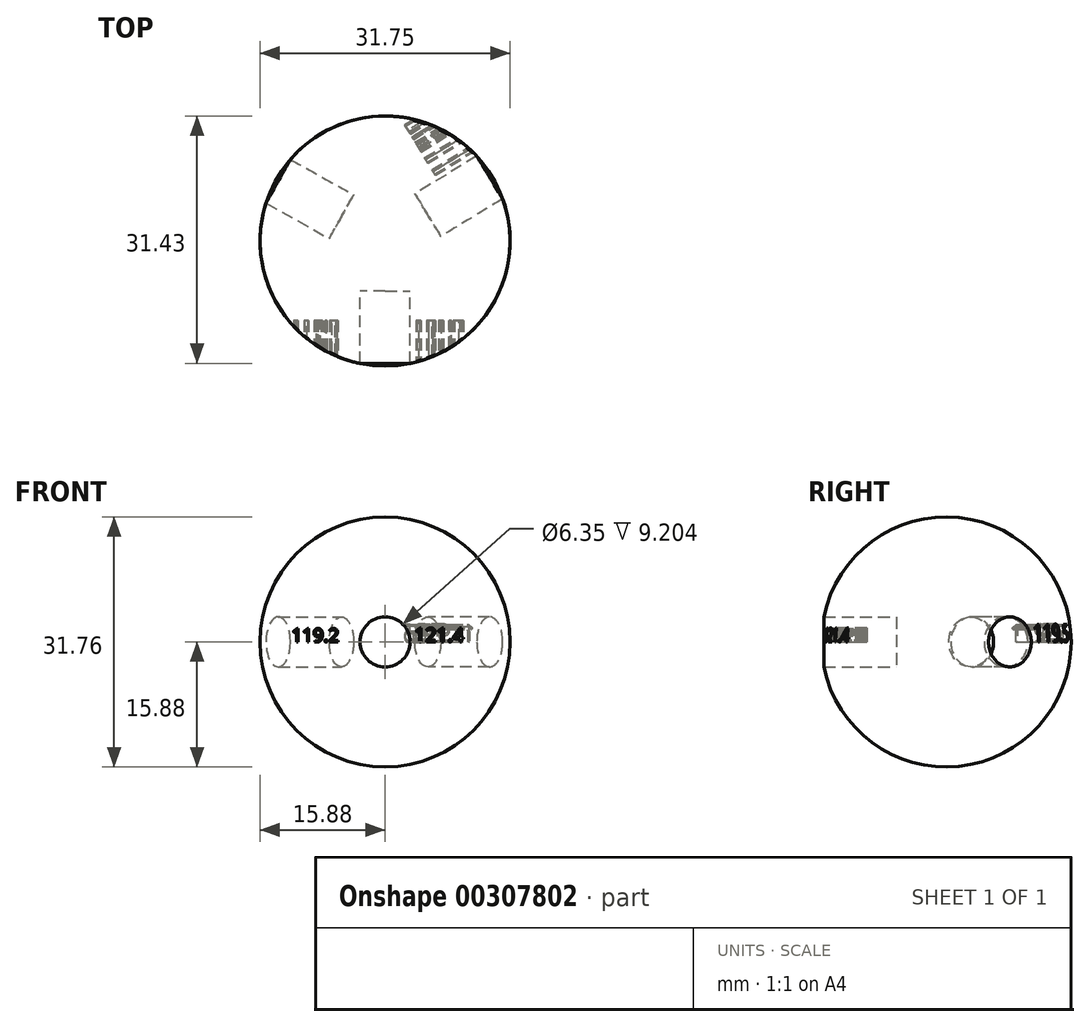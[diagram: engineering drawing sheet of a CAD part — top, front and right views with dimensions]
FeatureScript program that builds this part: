
annotation { "Feature Type Name" : "Feature", "Feature Type Description" : "" }
export const myFeature = defineFeature(function(context is Context, id is Id, definition is map)
    precondition{}
    {
        {
            var Q0;
            Q0=qCreatedBy(makeId("Top.planeOp"),FACE);
            var sketch = newSketch(context, id + "F0", { "sketchPlane" : qUnion([Q0])});
            skArc(sketch, "E0", {"start": v(0, 15.88) * mm, "mid": v(-15.88, 0) * mm, "end": v(0, -15.88) * mm});
            skLineSegment(sketch, "E1", {"start": v(0, 15.88) * mm, "end": v(0, -15.88) * mm});
            skSolve(sketch);
        }
        {
            var Q0;
            Q0=makeQuery(id+"F0.imprint","IMPRINT",FACE,{"disambiguationData":[TD([[makeQuery(id+"F0.imprint","IMPRINT",EDGE,{"derivedFrom":sQuery(id+"F0.wireOp",EDGE,"E0")}),1.0]])]});
            var Q1;
            Q1=sQuery(id+"F0.wireOp",EDGE,"E1");
            revolve(context, id + "F1", {"entities" : qUnion([Q0]), "axis" : qUnion([Q1]), "revolveType" : RevolveType.FULL});
        }
        {
            var Q0;
            Q0=qCreatedBy(makeId("Front.planeOp"),FACE);
            var sketch = newSketch(context, id + "F2", { "sketchPlane" : qUnion([Q0])});
            skLineSegment(sketch, "E2", {"start": v(0, 0) * mm, "end": v(0, 56.8) * mm, "construction": true});
            skLineSegment(sketch, "E3", {"start": v(0, 0) * mm, "end": v(75.92, 0) * mm, "construction": true});
            skSolve(sketch);
        }
        {
            var Q0;
            Q0=qCreatedBy(makeId("Front.planeOp"),FACE);
            cPlane(context, id + "F3", {"entities" : qUnion([Q0]), "cplaneType" : CPlaneType.OFFSET, "offset" : 6.35 * mm, "width" : 152.4 * mm, "height" : 152.4 * mm});
        }
        {
            var Q0;
            Q0=qCreatedBy(id+"F3.planeOp",FACE);
            var sketch = newSketch(context, id + "F4", { "sketchPlane" : qUnion([Q0])});
            skCircle(sketch, "E4", {"center": v(0, 0) * mm, "radius": 3.18 * mm});
            skSolve(sketch);
        }
        {
            var Q0;
            Q0 = qSketchRegion(id + "F4", true);
            extrude(context, id + "F5", {"entities" : qUnion([Q0]), "depth" : 25.4 * mm});
        }
        {
            var Q0;
            Q0=makeQuery(id+"F5.opExtrude","SWEPT_BODY",BODY,{"disambiguationData":[OSD([sQuery(id+"F4.wireOp",EDGE,"E4")])]});
            var Q1;
            Q1=sQuery(id+"F2.wireOp",EDGE,"E2");
            transform(context, id + "F6", {"entities" : qUnion([Q0]), "transformType" : TransformType.ROTATION, "transformAxis" : qUnion([Q1]), "angle" : 119.2 * degree, "oppositeDirection" : true, "makeCopy" : true});
        }
        {
            var Q0;
            Q0=makeQuery(id+"F6.opPattern","COPY",BODY,{"derivedFrom":makeQuery(id+"F5.opExtrude","SWEPT_BODY",BODY,{"disambiguationData":[OSD([sQuery(id+"F4.wireOp",EDGE,"E4")])]}),"instanceName":"1"});
            var Q1;
            Q1=sQuery(id+"F2.wireOp",EDGE,"E2");
            transform(context, id + "F7", {"entities" : qUnion([Q0]), "transformType" : TransformType.ROTATION, "transformAxis" : qUnion([Q1]), "angle" : 119.5 * degree, "oppositeDirection" : true, "makeCopy" : true});
        }
        {
            var Q0;
            Q0=makeQuery(id+"F5.opExtrude","CAP_FACE",FACE,{"disambiguationData":[OSD([sQuery(id+"F4.wireOp",EDGE,"E4")])],"isStart":false});
            cPlane(context, id + "F8", {"entities" : qUnion([Q0]), "cplaneType" : CPlaneType.OFFSET, "offset" : 12.7 * mm, "oppositeDirection" : true, "width" : 152.4 * mm, "height" : 152.4 * mm});
        }
        {
            var Q0;
            Q0=qCreatedBy(id+"F8.planeOp",FACE);
            var sketch = newSketch(context, id + "F9", { "sketchPlane" : qUnion([Q0])});
            skText(sketch, "E5", { "text": "119.2", "fontName": "OpenSans-Regular.ttf"});
            skText(sketch, "E6", { "text": "121.4", "fontName": "OpenSans-Regular.ttf"});
            const initialGuessF9  = {"E5": [-0.01187, 0, 1, 0, 0.0017], "E6": [0.00372, 0, 1, 0, 0.00177]};
            skSetInitialGuess(sketch, initialGuessF9);
            skSolve(sketch);
        }
        {
            var Q0;
            Q0 = qSketchRegion(id + "F9", true);
            extrude(context, id + "F10", {"entities" : qUnion([Q0]), "operationType" : NewBodyOperationType.REMOVE, "oppositeDirection" : true, "depth" : 8.97 * mm});
        }
        {
            var Q0;
            Q0=makeQuery(id+"F7.opPattern","COPY",FACE,{"derivedFrom":makeQuery(id+"F6.opPattern","COPY",FACE,{"derivedFrom":makeQuery(id+"F5.opExtrude","CAP_FACE",FACE,{"disambiguationData":[OSD([sQuery(id+"F4.wireOp",EDGE,"E4")])],"isStart":false}),"instanceName":"1"}),"instanceName":"1"});
            cPlane(context, id + "F11", {"entities" : qUnion([Q0]), "cplaneType" : CPlaneType.OFFSET, "offset" : 12.7 * mm, "oppositeDirection" : true, "width" : 152.4 * mm, "height" : 152.4 * mm});
        }
        {
            var Q0;
            Q0=qCreatedBy(id+"F11.planeOp",FACE);
            var sketch = newSketch(context, id + "F12", { "sketchPlane" : qUnion([Q0])});
            skText(sketch, "E7", { "text": "119.5", "fontName": "OpenSans-Regular.ttf"});
            const initialGuessF12  = {"E7": [0.00356, 0, 1, 0, 0.00225]};
            skSetInitialGuess(sketch, initialGuessF12);
            skSolve(sketch);
        }
        {
            var Q0;
            Q0 = qSketchRegion(id + "F12", true);
            extrude(context, id + "F13", {"entities" : qUnion([Q0]), "operationType" : NewBodyOperationType.REMOVE, "oppositeDirection" : true, "depth" : 9.25 * mm});
        }
        {
            var Q0;
            Q0=makeQuery(id+"F6.opPattern","COPY",BODY,{"derivedFrom":makeQuery(id+"F5.opExtrude","SWEPT_BODY",BODY,{"disambiguationData":[OSD([sQuery(id+"F4.wireOp",EDGE,"E4")])]}),"instanceName":"1"});
            var Q1;
            Q1=makeQuery(id+"F5.opExtrude","SWEPT_BODY",BODY,{"disambiguationData":[OSD([sQuery(id+"F4.wireOp",EDGE,"E4")])]});
            var Q2;
            Q2=makeQuery(id+"F7.opPattern","COPY",BODY,{"derivedFrom":makeQuery(id+"F6.opPattern","COPY",BODY,{"derivedFrom":makeQuery(id+"F5.opExtrude","SWEPT_BODY",BODY,{"disambiguationData":[OSD([sQuery(id+"F4.wireOp",EDGE,"E4")])]}),"instanceName":"1"}),"instanceName":"1"});
            var Q3;
            Q3=makeQuery(id+"F1.opRevolve","SWEPT_BODY",BODY,{"disambiguationData":[OSD([sQuery(id+"F0.wireOp",EDGE,"E0"),sQuery(id+"F0.wireOp",EDGE,"E1")])]});
            booleanBodies(context, id + "F14", {"operationType" : BooleanOperationType.SUBTRACTION, "tools" : qUnion([Q0, Q1, Q2]), "targets" : qUnion([Q3])});
        }
    });
